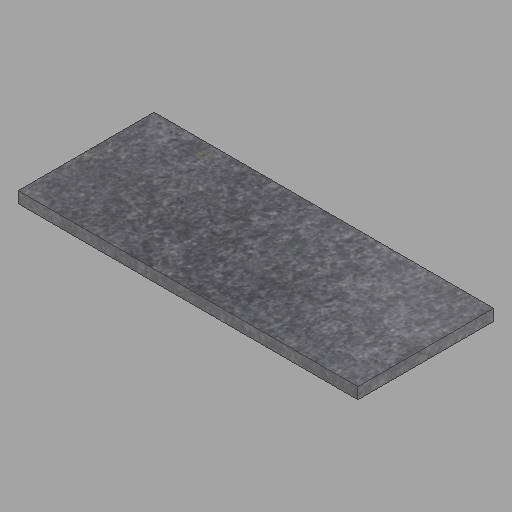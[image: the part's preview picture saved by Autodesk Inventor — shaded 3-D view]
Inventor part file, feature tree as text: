
AUTODESK INVENTOR PART (.ipt)
format: ipt  version: 2023 (Build 270158000, 158)  size: 208,384 bytes
history: native  units: in
note: dims shown in document units (in); Inventor stores cm internally (conversion verified against a paired STEP export)
features: other x1, extrude x1, sketch x1
ambient origin geometry x8: Origin, YZ Plane, XZ Plane, XY Plane, X Axis, Y Axis, Z Axis, Center Point
bodies: Solid1 (feature_tree)
feature tree (3):
  other  "2x24x60-2"
  extrude  "Extrusion1"  Depth=24.0in
  sketch  "Sketch1"  dims[d0=2.0in d1=24.0in d2=60.0in d3=0.0in]
